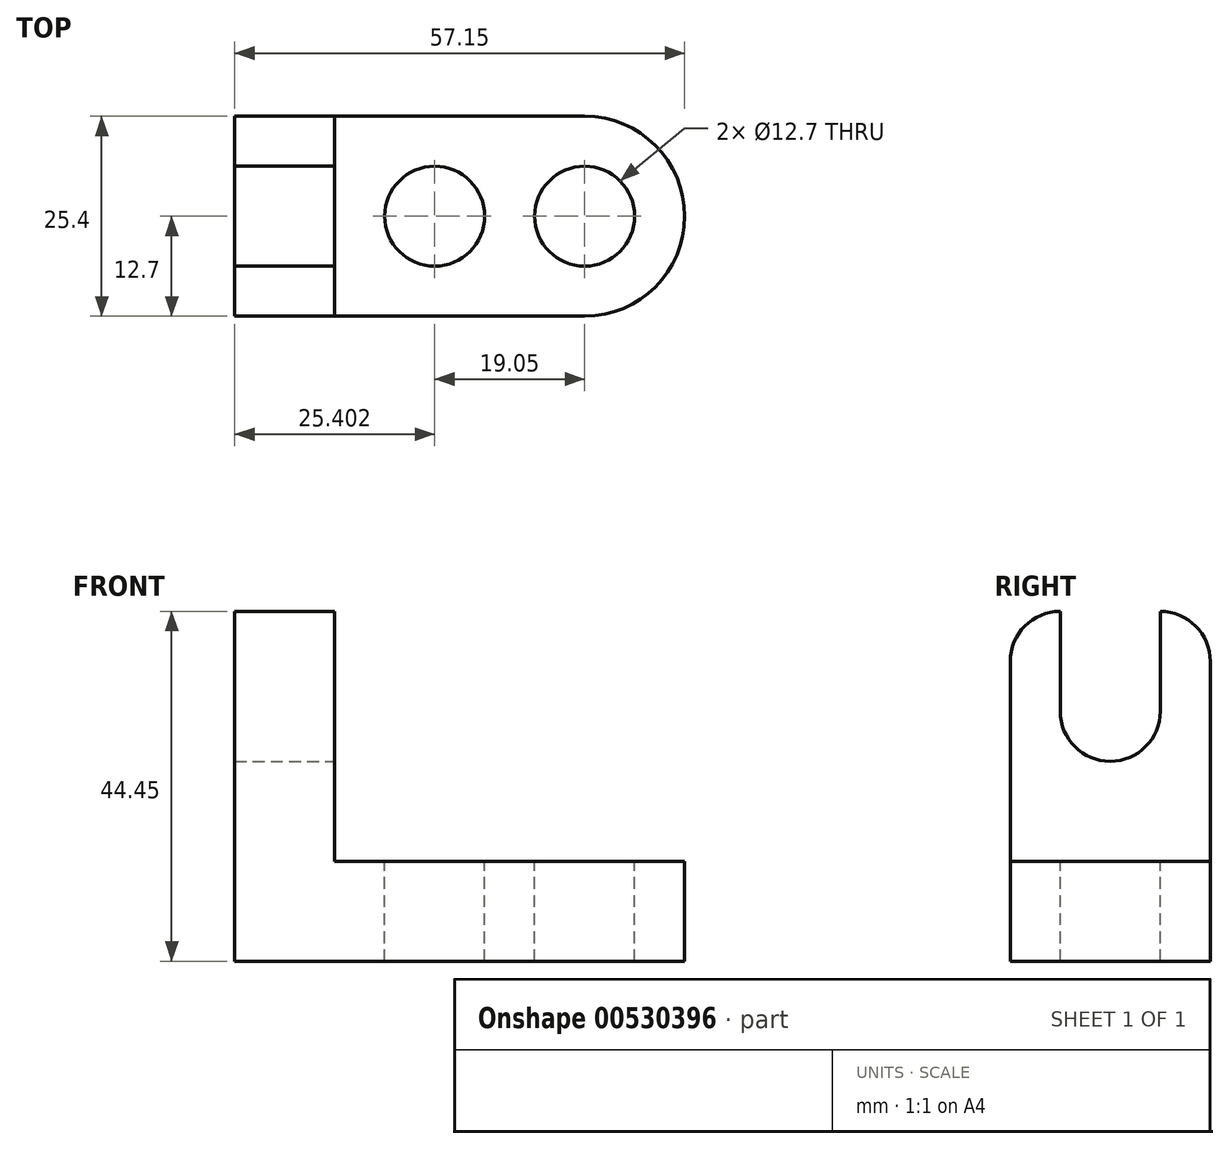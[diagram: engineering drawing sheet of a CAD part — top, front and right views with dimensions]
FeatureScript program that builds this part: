
annotation { "Feature Type Name" : "Feature", "Feature Type Description" : "" }
export const myFeature = defineFeature(function(context is Context, id is Id, definition is map)
    precondition{}
    {
        {
            var Q0;
            Q0=qCreatedBy(makeId("Front.planeOp"),FACE);
            var sketch = newSketch(context, id + "F0", { "sketchPlane" : qUnion([Q0])});
            skLineSegment(sketch, "E0", {"start": v(-44.67, 44.45) * mm, "end": v(-44.67, 0) * mm});
            skLineSegment(sketch, "E1", {"start": v(-44.67, 0) * mm, "end": v(12.48, 0) * mm});
            skLineSegment(sketch, "E2", {"start": v(12.48, 0) * mm, "end": v(12.48, 12.7) * mm});
            skLineSegment(sketch, "E3", {"start": v(12.48, 12.7) * mm, "end": v(-31.97, 12.7) * mm});
            skLineSegment(sketch, "E4", {"start": v(-31.97, 12.7) * mm, "end": v(-31.97, 44.45) * mm});
            skLineSegment(sketch, "E5", {"start": v(-31.97, 44.45) * mm, "end": v(-44.67, 44.45) * mm});
            skSolve(sketch);
        }
        {
            var Q0;
            Q0 = qSketchRegion(id + "F0", true);
            extrude(context, id + "F1", {"entities" : qUnion([Q0]), "depth" : 25.4 * mm, "offsetDistance" : 25.4 * mm});
        }
        {
            var Q0;
            Q0=makeQuery(id+"F1.opExtrude","SWEPT_FACE",FACE,{"disambiguationData":[OSD([sQuery(id+"F0.wireOp",EDGE,"E4")])]});
            var sketch = newSketch(context, id + "F2", { "sketchPlane" : qUnion([Q0])});
            skLineSegment(sketch, "E6", {"start": v(-25.4, 12.7) * mm, "end": v(-25.4, 38.1) * mm});
            skLineSegment(sketch, "E7", {"start": v(-25.4, 38.1) * mm, "end": v(-25.4, 44.45) * mm});
            skLineSegment(sketch, "E8", {"start": v(-25.4, 44.45) * mm, "end": v(0, 44.45) * mm});
            skLineSegment(sketch, "E9", {"start": v(0, 12.7) * mm, "end": v(0, 25.4) * mm});
            skPoint(sketch, "E9.endSnap0", {"position": v(-25.4, 25.4) * mm});
            skLineSegment(sketch, "E10", {"start": v(0, 25.4) * mm, "end": v(-25.4, 25.4) * mm});
            skLineSegment(sketch, "E11", {"start": v(-12.7, 44.45) * mm, "end": v(-12.7, 12.7) * mm});
            skLineSegment(sketch, "E12", {"start": v(-25.4, 44.45) * mm, "end": v(-12.7, 44.45) * mm});
            skLineSegment(sketch, "E13", {"start": v(-12.7, 44.45) * mm, "end": v(0, 44.45) * mm});
            skLineSegment(sketch, "E14", {"start": v(-25.4, 44.45) * mm, "end": v(-19.05, 44.45) * mm});
            skArc(sketch, "E15", {"start": v(-19.05, 44.45) * mm, "mid": v(-23.54, 42.6) * mm, "end": v(-25.4, 38.1) * mm});
            skArc(sketch, "E16", {"start": v(0, 38.1) * mm, "mid": v(-1.86, 42.6) * mm, "end": v(-6.35, 44.45) * mm});
            skSolve(sketch);
        }
        {
            var Q0;
            Q0=makeQuery(id+"F2.imprint","IMPRINT",FACE,{"disambiguationData":[TD([[makeQuery(id+"F2.imprint","IMPRINT",EDGE,{"derivedFrom":sQuery(id+"F2.wireOp",EDGE,"E7")}),-1.0]])]});
            var Q1;
            {var subQ3=sQuery(id+"F2.wireOp",EDGE,"E16");Q1=makeQuery(id+"F2.imprint","IMPRINT",FACE,{"disambiguationData":[TD([[makeQuery(id+"F2.imprint","IMPRINT",EDGE,{"derivedFrom":subQ3}),-1.0]])]});}
            extrude(context, id + "F3", {"entities" : qUnion([Q0, Q1]), "operationType" : NewBodyOperationType.REMOVE, "endBound" : BoundingType.THROUGH_ALL, "oppositeDirection" : true, "depth" : 25.4 * mm, "offsetDistance" : 25.4 * mm});
        }
        {
            var Q0;
            Q0=makeQuery(id+"F1.opExtrude","SWEPT_FACE",FACE,{"disambiguationData":[OSD([sQuery(id+"F0.wireOp",EDGE,"E4")])]});
            var sketch = newSketch(context, id + "F4", { "sketchPlane" : qUnion([Q0])});
            skLineSegment(sketch, "E17", {"start": v(-19.05, 44.45) * mm, "end": v(-19.05, 31.75) * mm});
            skLineSegment(sketch, "E18", {"start": v(-19.05, 31.75) * mm, "end": v(-6.35, 31.75) * mm});
            skLineSegment(sketch, "E19", {"start": v(-6.35, 31.75) * mm, "end": v(-6.35, 44.45) * mm});
            skLineSegment(sketch, "E20", {"start": v(-6.35, 44.45) * mm, "end": v(-19.05, 44.45) * mm});
            skCircle(sketch, "E21", {"center": v(-12.7, 31.75) * mm, "radius": 6.35 * mm});
            skSolve(sketch);
        }
        {
            var Q0;
            {var subQ0=sQuery(id+"F4.wireOp",EDGE,"E17");Q0=makeQuery(id+"F4.imprint","IMPRINT",FACE,{"disambiguationData":[TD([[makeQuery(id+"F4.imprint","IMPRINT",EDGE,{"derivedFrom":subQ0}),1.0]])]});}
            var Q1;
            {var subQ0=sQuery(id+"F4.wireOp",EDGE,"E18");Q1=makeQuery(id+"F4.imprint","IMPRINT",FACE,{"disambiguationData":[TD([[makeQuery(id+"F4.imprint","IMPRINT",EDGE,{"derivedFrom":subQ0}),-1.0]])]});}
            var Q2;
            {var subQ0=sQuery(id+"F4.wireOp",EDGE,"E18");Q2=makeQuery(id+"F4.imprint","IMPRINT",FACE,{"disambiguationData":[TD([[makeQuery(id+"F4.imprint","IMPRINT",EDGE,{"derivedFrom":subQ0}),1.0]])]});}
            extrude(context, id + "F5", {"entities" : qUnion([Q0, Q1, Q2]), "operationType" : NewBodyOperationType.REMOVE, "endBound" : BoundingType.THROUGH_ALL, "oppositeDirection" : true, "depth" : 25.4 * mm, "offsetDistance" : 25.4 * mm});
        }
        {
            var Q0;
            Q0=makeQuery(id+"F1.opExtrude","SWEPT_FACE",FACE,{"disambiguationData":[OSD([sQuery(id+"F0.wireOp",EDGE,"E3")])]});
            var sketch = newSketch(context, id + "F6", { "sketchPlane" : qUnion([Q0])});
            skLineSegment(sketch, "E22", {"start": v(-31.97, 0) * mm, "end": v(-31.97, -12.7) * mm});
            skLineSegment(sketch, "E23", {"start": v(-31.97, -12.7) * mm, "end": v(-31.97, -25.4) * mm});
            skLineSegment(sketch, "E24", {"start": v(-31.97, -12.7) * mm, "end": v(12.48, -12.7) * mm});
            skLineSegment(sketch, "E25", {"start": v(-31.97, 0) * mm, "end": v(-0.22, 0) * mm});
            skLineSegment(sketch, "E26", {"start": v(-0.22, 0) * mm, "end": v(12.48, 0) * mm});
            skLineSegment(sketch, "E27", {"start": v(-0.22, 0) * mm, "end": v(-0.22, -25.4) * mm});
            skArc(sketch, "E28", {"start": v(-0.22, -25.4) * mm, "mid": v(12.48, -12.7) * mm, "end": v(-0.22, 0) * mm});
            skCircle(sketch, "E29", {"center": v(-19.27, -12.7) * mm, "radius": 6.35 * mm});
            skCircle(sketch, "E30", {"center": v(-0.22, -12.7) * mm, "radius": 6.35 * mm});
            skSolve(sketch);
        }
        {
            var Q0;
            {var subQ0=sQuery(id+"F6.wireOp",EDGE,"E26");Q0=makeQuery(id+"F6.imprint","IMPRINT",FACE,{"disambiguationData":[TD([[makeQuery(id+"F6.imprint","IMPRINT",EDGE,{"derivedFrom":subQ0}),1.0]])]});}
            var Q1;
            {var subQ1=sQuery(id+"F0.wireOp",EDGE,"E3");var subQ2=makeQuery(id+"F1.opExtrude","SWEPT_EDGE",EDGE,{"disambiguationData":[OSD([sQuery(id+"F0.wireOp",EDGE,"E2"),subQ1])]});var subQ4=makeQuery(id+"F1.opExtrude","CAP_EDGE",EDGE,{"disambiguationData":[OSD([subQ1])],"isStart":false});var subQ6=makeQuery(id+"F6.imprint","INTERSECT",VERTEX,{"derivedFrom":[subQ2,subQ4]});Q1=makeQuery(id+"F6.imprint","IMPRINT",FACE,{"disambiguationData":[TD([[makeQuery(id+"F6.imprint","IMPRINT",EDGE,{"disambiguationData":[TD([[subQ6,-1.0]])],"derivedFrom":subQ4}),-1.0]])]});}
            var Q2;
            {var subQ0=sQuery(id+"F6.wireOp",EDGE,"E29");var subQ1=sQuery(id+"F6.wireOp",EDGE,"E24");var subQ2=makeQuery(id+"F6.imprint","INTERSECT",VERTEX,{"disambiguationData":[OD(0.0)],"derivedFrom":[subQ1,subQ0]});Q2=makeQuery(id+"F6.imprint","IMPRINT",FACE,{"disambiguationData":[TD([[makeQuery(id+"F6.imprint","IMPRINT",EDGE,{"disambiguationData":[TD([[subQ2,-1.0]])],"derivedFrom":subQ1}),1.0]])]});}
            var Q3;
            {var subQ0=sQuery(id+"F6.wireOp",EDGE,"E29");var subQ1=sQuery(id+"F6.wireOp",EDGE,"E24");var subQ2=makeQuery(id+"F6.imprint","INTERSECT",VERTEX,{"disambiguationData":[OD(0.0)],"derivedFrom":[subQ1,subQ0]});Q3=makeQuery(id+"F6.imprint","IMPRINT",FACE,{"disambiguationData":[TD([[makeQuery(id+"F6.imprint","IMPRINT",EDGE,{"disambiguationData":[TD([[subQ2,-1.0]])],"derivedFrom":subQ1}),-1.0]])]});}
            var Q4;
            {var subQ0=sQuery(id+"F6.wireOp",EDGE,"E30");var subQ1=sQuery(id+"F6.wireOp",EDGE,"E24");var subQ2=makeQuery(id+"F6.imprint","INTERSECT",VERTEX,{"disambiguationData":[OD(0.0)],"derivedFrom":[subQ1,subQ0]});Q4=makeQuery(id+"F6.imprint","IMPRINT",FACE,{"disambiguationData":[TD([[makeQuery(id+"F6.imprint","IMPRINT",EDGE,{"disambiguationData":[TD([[subQ2,-1.0]])],"derivedFrom":subQ1}),1.0]])]});}
            var Q5;
            {var subQ0=sQuery(id+"F6.wireOp",EDGE,"E27");var subQ1=sQuery(id+"F6.wireOp",EDGE,"E24");var subQ2=makeQuery(id+"F6.imprint","INTERSECT",VERTEX,{"derivedFrom":[subQ1,subQ0]});Q5=makeQuery(id+"F6.imprint","IMPRINT",FACE,{"disambiguationData":[TD([[makeQuery(id+"F6.imprint","IMPRINT",EDGE,{"disambiguationData":[TD([[subQ2,-1.0]])],"derivedFrom":subQ1}),1.0]])]});}
            var Q6;
            {var subQ0=sQuery(id+"F6.wireOp",EDGE,"E27");var subQ1=sQuery(id+"F6.wireOp",EDGE,"E24");var subQ2=makeQuery(id+"F6.imprint","INTERSECT",VERTEX,{"derivedFrom":[subQ1,subQ0]});Q6=makeQuery(id+"F6.imprint","IMPRINT",FACE,{"disambiguationData":[TD([[makeQuery(id+"F6.imprint","IMPRINT",EDGE,{"disambiguationData":[TD([[subQ2,-1.0]])],"derivedFrom":subQ1}),-1.0]])]});}
            var Q7;
            {var subQ0=sQuery(id+"F6.wireOp",EDGE,"E30");var subQ1=sQuery(id+"F6.wireOp",EDGE,"E24");var subQ2=makeQuery(id+"F6.imprint","INTERSECT",VERTEX,{"disambiguationData":[OD(0.0)],"derivedFrom":[subQ1,subQ0]});Q7=makeQuery(id+"F6.imprint","IMPRINT",FACE,{"disambiguationData":[TD([[makeQuery(id+"F6.imprint","IMPRINT",EDGE,{"disambiguationData":[TD([[subQ2,-1.0]])],"derivedFrom":subQ1}),-1.0]])]});}
            extrude(context, id + "F7", {"entities" : qUnion([Q0, Q1, Q2, Q3, Q4, Q5, Q6, Q7]), "operationType" : NewBodyOperationType.REMOVE, "endBound" : BoundingType.THROUGH_ALL, "oppositeDirection" : true, "depth" : 25.4 * mm, "offsetDistance" : 25.4 * mm});
        }
    });
